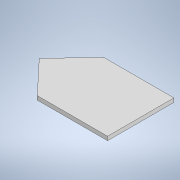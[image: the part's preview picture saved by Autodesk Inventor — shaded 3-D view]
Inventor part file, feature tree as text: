
AUTODESK INVENTOR PART (.ipt)
format: ipt  version: 2022 (Build 260153000, 153)  size: 92,160 bytes
history: native  units: in
note: dims shown in document units (in); Inventor stores cm internally (conversion verified against a paired STEP export)
features: extrude x1, sketch x1
ambient origin geometry x8: Origin, YZ Plane, XZ Plane, XY Plane, X Axis, Y Axis, Z Axis, Center Point
bodies: Solid1 (feature_tree)
feature tree (2):
  extrude  "Extrusion1"  Depth=3.3465in
  sketch  "Sketch1"  dims[d0=3.5433in d1=3.3465in d4=0.1969in d5=0.0in]
